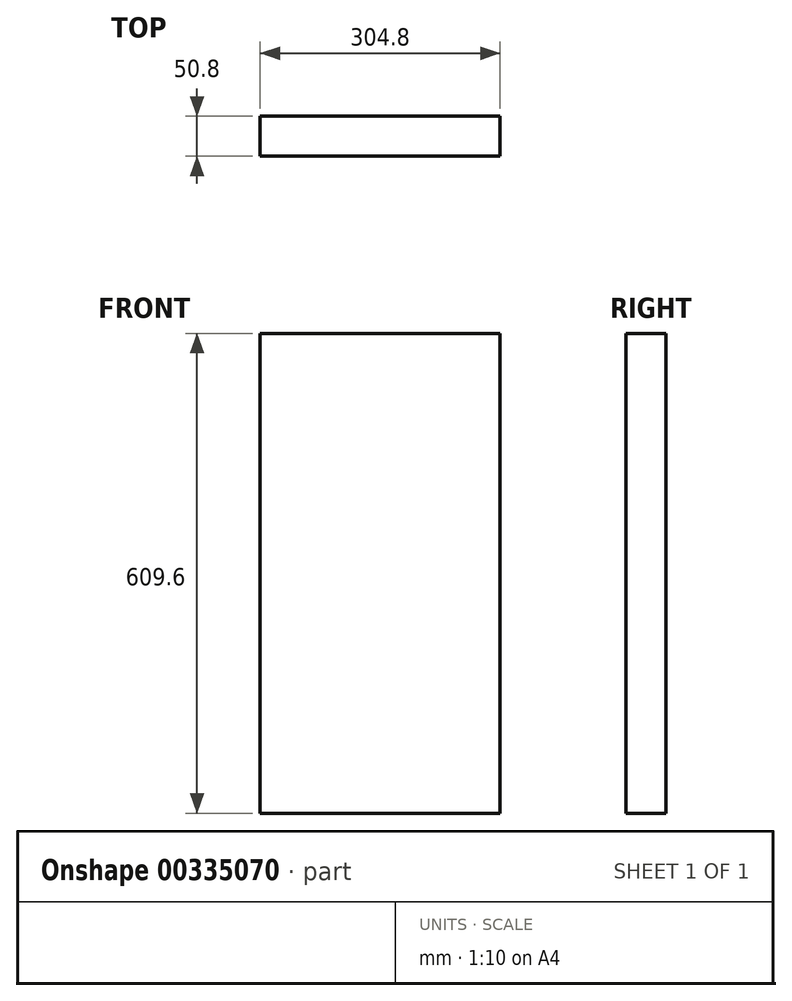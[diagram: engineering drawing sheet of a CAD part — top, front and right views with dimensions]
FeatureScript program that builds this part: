
annotation { "Feature Type Name" : "Feature", "Feature Type Description" : "" }
export const myFeature = defineFeature(function(context is Context, id is Id, definition is map)
    precondition{}
    {
        {
            var Q0;
            Q0=qCreatedBy(makeId("Front.planeOp"),FACE);
            var sketch = newSketch(context, id + "F0", { "sketchPlane" : qUnion([Q0])});
            skLineSegment(sketch, "E0", {"start": v(-155.02, 554.45) * mm, "end": v(149.78, 554.45) * mm});
            skLineSegment(sketch, "E1", {"start": v(-155.02, 554.45) * mm, "end": v(-155.02, -55.15) * mm});
            skLineSegment(sketch, "E2", {"start": v(-155.02, -55.15) * mm, "end": v(149.78, -55.15) * mm});
            skLineSegment(sketch, "E3", {"start": v(149.78, -55.15) * mm, "end": v(149.78, 554.45) * mm});
            skSolve(sketch);
        }
        {
            var Q0;
            Q0=makeQuery(id+"F0.imprint","IMPRINT",FACE,{"disambiguationData":[TD([[makeQuery(id+"F0.imprint","IMPRINT",EDGE,{"derivedFrom":sQuery(id+"F0.wireOp",EDGE,"E0")}),-1.0]])]});
            extrude(context, id + "F1", {"entities" : qUnion([Q0]), "depth" : 50.8 * mm});
        }
    });
